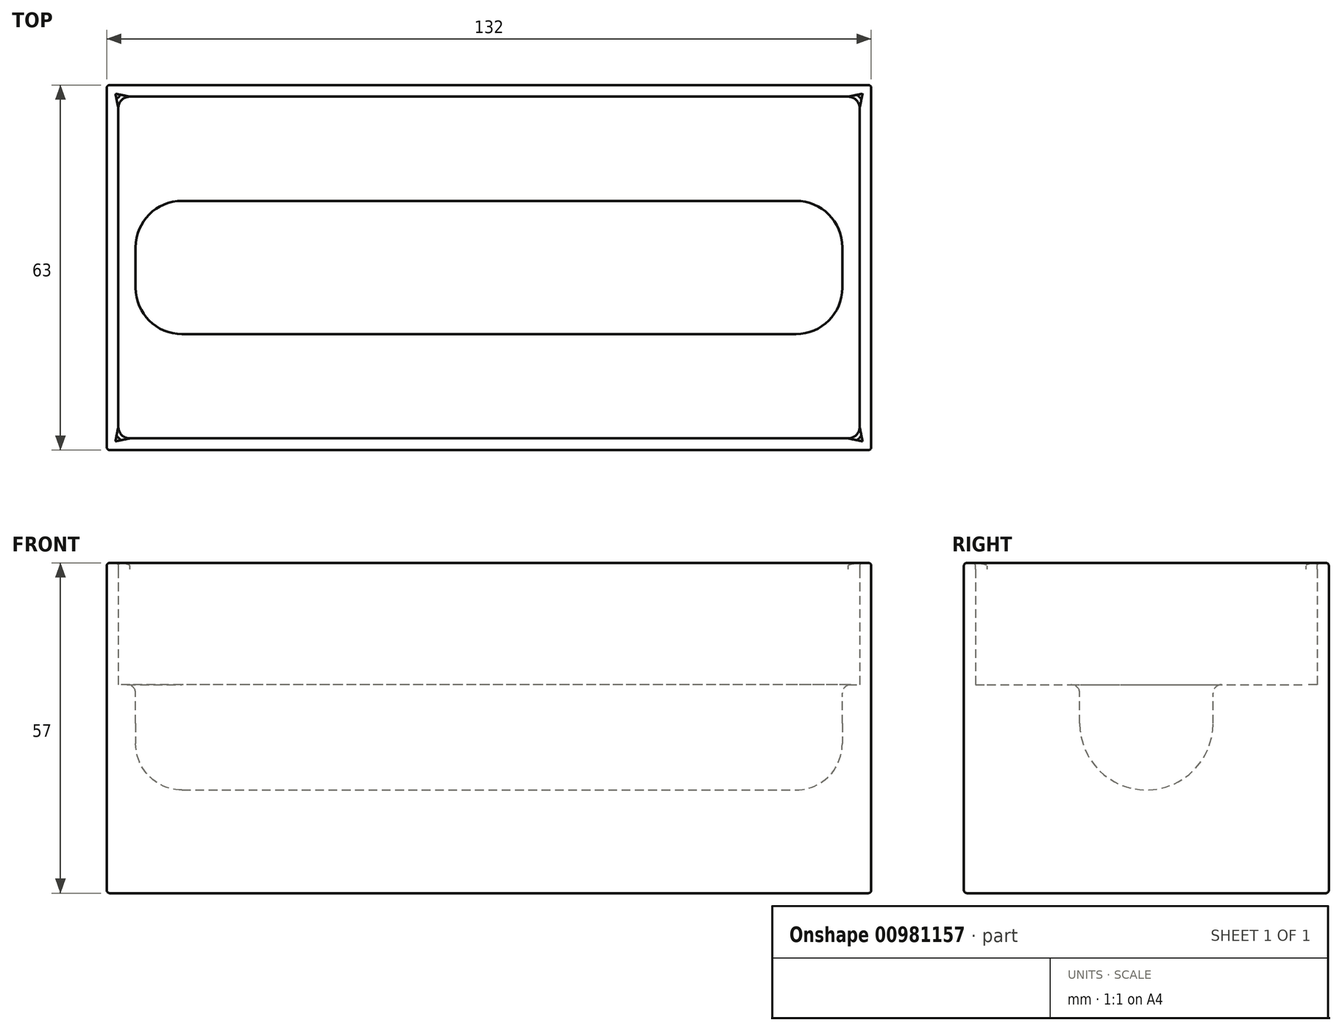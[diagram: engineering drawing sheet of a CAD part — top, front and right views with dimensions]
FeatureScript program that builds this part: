
annotation { "Feature Type Name" : "Feature", "Feature Type Description" : "" }
export const myFeature = defineFeature(function(context is Context, id is Id, definition is map)
    precondition{}
    {
        {
            var Q0;
            Q0=qCreatedBy(makeId("Top.planeOp"),FACE);
            var sketch = newSketch(context, id + "F0", { "sketchPlane" : qUnion([Q0])});
            skLineSegment(sketch, "E0.bottom", {"start": v(66, -31.5) * mm, "end": v(-66, -31.5) * mm});
            skLineSegment(sketch, "E0.top", {"start": v(66, 31.5) * mm, "end": v(-66, 31.5) * mm});
            skLineSegment(sketch, "E0.left", {"start": v(66, -31.5) * mm, "end": v(66, 31.5) * mm});
            skLineSegment(sketch, "E0.right", {"start": v(-66, -31.5) * mm, "end": v(-66, 31.5) * mm});
            skPoint(sketch, "E0.middle", {"position": v(0, 0) * mm});
            skLineSegment(sketch, "E1.bottom", {"start": v(64, -29.5) * mm, "end": v(-64, -29.5) * mm});
            skLineSegment(sketch, "E1.top", {"start": v(64, 29.5) * mm, "end": v(-64, 29.5) * mm});
            skLineSegment(sketch, "E1.left", {"start": v(64, -29.5) * mm, "end": v(64, 29.5) * mm});
            skLineSegment(sketch, "E1.right", {"start": v(-64, -29.5) * mm, "end": v(-64, 29.5) * mm});
            skSolve(sketch);
        }
        {
            var Q0;
            Q0=makeQuery(id+"F0.imprint","IMPRINT",FACE,{"disambiguationData":[TD([[makeQuery(id+"F0.imprint","IMPRINT",EDGE,{"derivedFrom":sQuery(id+"F0.wireOp",EDGE,"E0.bottom")}),-1.0]])]});
            extrude(context, id + "F1", {"entities" : qUnion([Q0]), "depth" : 57 * mm, "offsetDistance" : 25 * mm});
        }
        {
            var Q0;
            Q0=makeQuery(id+"F0.imprint","IMPRINT",FACE,{"disambiguationData":[TD([[makeQuery(id+"F0.imprint","IMPRINT",EDGE,{"derivedFrom":sQuery(id+"F0.wireOp",EDGE,"E1.bottom")}),-1.0]])]});
            extrude(context, id + "F2", {"entities" : qUnion([Q0]), "operationType" : NewBodyOperationType.ADD, "depth" : 36 * mm, "offsetDistance" : 25 * mm});
        }
        {
            var Q0;
            Q0=qCreatedBy(makeId("Right.planeOp"),FACE);
            var sketch = newSketch(context, id + "F3", { "sketchPlane" : qUnion([Q0])});
            skLineSegment(sketch, "E2.bottom", {"start": v(-11.5, 29.3) * mm, "end": v(11.5, 29.3) * mm});
            skLineSegment(sketch, "E2.top", {"start": v(-11.5, 52.3) * mm, "end": v(11.5, 52.3) * mm});
            skLineSegment(sketch, "E2.left", {"start": v(-11.5, 29.3) * mm, "end": v(-11.5, 52.3) * mm});
            skLineSegment(sketch, "E2.right", {"start": v(11.5, 29.3) * mm, "end": v(11.5, 52.3) * mm});
            skPoint(sketch, "E2.middle", {"position": v(0, 40.8) * mm});
            skArc(sketch, "E3", {"start": v(-11.5, 29.3) * mm, "mid": v(0, 17.8) * mm, "end": v(11.5, 29.3) * mm});
            skSolve(sketch);
        }
        {
            var Q0;
            Q0 = qSketchRegion(id + "F3", true);
            extrude(context, id + "F4", {"entities" : qUnion([Q0]), "operationType" : NewBodyOperationType.REMOVE, "oppositeDirection" : true, "depth" : 122 * mm, "offsetDistance" : 25 * mm, "symmetric" : true});
        }
        {
            var Q0;
            Q0=makeQuery(id+"F4.boolean.opBoolean","COPY",EDGE,{"derivedFrom":makeQuery(id+"F4.opExtrude","CAP_EDGE",EDGE,{"disambiguationData":[OSD([sQuery(id+"F3.wireOp",EDGE,"E3")])],"isStart":false})});
            var Q1;
            Q1=makeQuery(id+"F4.boolean.opBoolean","COPY",EDGE,{"derivedFrom":makeQuery(id+"F4.opExtrude","CAP_EDGE",EDGE,{"disambiguationData":[OSD([sQuery(id+"F3.wireOp",EDGE,"E3")])],"isStart":true})});
            fillet(context, id + "F5", {"entities" : qUnion([Q0, Q1]), "tangentPropagation" : true, "radius" : 8 * mm, "defaultsChanged" : false, "vertexSettings" : [], "allowEdgeOverflow" : false});
        }
        {
            var Q0;
            Q0=makeQuery(id+"F4.boolean.opBoolean","INTERSECT",EDGE,{"derivedFrom":[makeQuery(id+"F2.opExtrude","CAP_FACE",FACE,{"disambiguationData":[OSD([sQuery(id+"F0.wireOp",EDGE,"E1.bottom"),sQuery(id+"F0.wireOp",EDGE,"E1.top"),sQuery(id+"F0.wireOp",EDGE,"E1.left"),sQuery(id+"F0.wireOp",EDGE,"E1.right")])],"isStart":false}),makeQuery(id+"F4.opExtrude","SWEPT_FACE",FACE,{"disambiguationData":[OSD([sQuery(id+"F3.wireOp",EDGE,"E2.right")])]})]});
            fillet(context, id + "F6", {"entities" : qUnion([Q0]), "tangentPropagation" : true, "radius" : 1.5 * mm, "defaultsChanged" : false, "vertexSettings" : [], "allowEdgeOverflow" : false});
        }
        {
            var Q0;
            Q0=makeQuery(id+"F1.opExtrude","CAP_EDGE",EDGE,{"disambiguationData":[OSD([sQuery(id+"F0.wireOp",EDGE,"E1.top")])],"isStart":false});
            var Q1;
            Q1=makeQuery(id+"F1.opExtrude","CAP_EDGE",EDGE,{"disambiguationData":[OSD([sQuery(id+"F0.wireOp",EDGE,"E1.right")])],"isStart":false});
            var Q2;
            Q2=makeQuery(id+"F1.opExtrude","CAP_EDGE",EDGE,{"disambiguationData":[OSD([sQuery(id+"F0.wireOp",EDGE,"E1.bottom")])],"isStart":false});
            var Q3;
            Q3=makeQuery(id+"F2.opExtrude","CAP_EDGE",EDGE,{"disambiguationData":[OSD([sQuery(id+"F0.wireOp",EDGE,"E1.left")])],"isStart":false});
            var Q4;
            Q4=makeQuery(id+"F1.opExtrude","CAP_EDGE",EDGE,{"disambiguationData":[OSD([sQuery(id+"F0.wireOp",EDGE,"E0.right")])],"isStart":false});
            var Q5;
            Q5=makeQuery(id+"F1.opExtrude","CAP_EDGE",EDGE,{"disambiguationData":[OSD([sQuery(id+"F0.wireOp",EDGE,"E0.top")])],"isStart":false});
            var Q6;
            Q6=makeQuery(id+"F1.opExtrude","CAP_EDGE",EDGE,{"disambiguationData":[OSD([sQuery(id+"F0.wireOp",EDGE,"E0.bottom")])],"isStart":false});
            var Q7;
            Q7=makeQuery(id+"F1.opExtrude","CAP_EDGE",EDGE,{"disambiguationData":[OSD([sQuery(id+"F0.wireOp",EDGE,"E0.left")])],"isStart":false});
            var Q8;
            Q8=makeQuery(id+"F1.opExtrude","SWEPT_EDGE",EDGE,{"disambiguationData":[OSD([sQuery(id+"F0.wireOp",EDGE,"E0.bottom"),sQuery(id+"F0.wireOp",EDGE,"E0.right")])]});
            var Q9;
            Q9=makeQuery(id+"F1.opExtrude","SWEPT_EDGE",EDGE,{"disambiguationData":[OSD([sQuery(id+"F0.wireOp",EDGE,"E0.bottom"),sQuery(id+"F0.wireOp",EDGE,"E0.left")])]});
            var Q10;
            Q10=makeQuery(id+"F1.opExtrude","CAP_EDGE",EDGE,{"disambiguationData":[OSD([sQuery(id+"F0.wireOp",EDGE,"E0.bottom")])],"isStart":true});
            var Q11;
            Q11=makeQuery(id+"F1.opExtrude","CAP_EDGE",EDGE,{"disambiguationData":[OSD([sQuery(id+"F0.wireOp",EDGE,"E0.right")])],"isStart":true});
            var Q12;
            Q12=makeQuery(id+"F1.opExtrude","SWEPT_FACE",FACE,{"disambiguationData":[OSD([sQuery(id+"F0.wireOp",EDGE,"E0.right")])]});
            var Q13;
            Q13=makeQuery(id+"F1.opExtrude","SWEPT_EDGE",EDGE,{"disambiguationData":[OSD([sQuery(id+"F0.wireOp",EDGE,"E0.top"),sQuery(id+"F0.wireOp",EDGE,"E0.left")])]});
            var Q14;
            Q14=makeQuery(id+"F1.opExtrude","CAP_EDGE",EDGE,{"disambiguationData":[OSD([sQuery(id+"F0.wireOp",EDGE,"E0.left")])],"isStart":true});
            var Q15;
            Q15=makeQuery(id+"F1.opExtrude","CAP_EDGE",EDGE,{"disambiguationData":[OSD([sQuery(id+"F0.wireOp",EDGE,"E0.top")])],"isStart":true});
            var Q16;
            Q16=makeQuery(id+"F2.opExtrude","CAP_EDGE",EDGE,{"disambiguationData":[OSD([sQuery(id+"F0.wireOp",EDGE,"E1.right")])],"isStart":false});
            var Q17;
            Q17=makeQuery(id+"F1.opExtrude","CAP_EDGE",EDGE,{"disambiguationData":[OSD([sQuery(id+"F0.wireOp",EDGE,"E1.left")])],"isStart":false});
            fillet(context, id + "F7", {"entities" : qUnion([Q0, Q1, Q2, Q3, Q4, Q5, Q6, Q7, Q8, Q9, Q10, Q11, Q12, Q13, Q14, Q15, Q16, Q17]), "tangentPropagation" : true, "radius" : .5 * mm, "defaultsChanged" : false, "vertexSettings" : [], "allowEdgeOverflow" : false});
        }
        {
            var Q0;
            Q0=makeQuery(id+"F1.opExtrude","SWEPT_EDGE",EDGE,{"disambiguationData":[OSD([sQuery(id+"F0.wireOp",EDGE,"E1.top"),sQuery(id+"F0.wireOp",EDGE,"E1.right")])]});
            var Q1;
            Q1=makeQuery(id+"F1.opExtrude","SWEPT_EDGE",EDGE,{"disambiguationData":[OSD([sQuery(id+"F0.wireOp",EDGE,"E1.bottom"),sQuery(id+"F0.wireOp",EDGE,"E1.right")])]});
            var Q2;
            Q2=makeQuery(id+"F1.opExtrude","SWEPT_EDGE",EDGE,{"disambiguationData":[OSD([sQuery(id+"F0.wireOp",EDGE,"E1.top"),sQuery(id+"F0.wireOp",EDGE,"E1.left")])]});
            var Q3;
            Q3=makeQuery(id+"F1.opExtrude","SWEPT_EDGE",EDGE,{"disambiguationData":[OSD([sQuery(id+"F0.wireOp",EDGE,"E1.bottom"),sQuery(id+"F0.wireOp",EDGE,"E1.left")])]});
            fillet(context, id + "F8", {"entities" : qUnion([Q0, Q1, Q2, Q3]), "tangentPropagation" : true, "radius" : 2 * mm, "defaultsChanged" : false, "vertexSettings" : [], "allowEdgeOverflow" : false});
        }
    });
